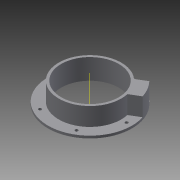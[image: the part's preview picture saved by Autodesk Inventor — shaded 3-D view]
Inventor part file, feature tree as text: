
AUTODESK INVENTOR PART (.ipt)
format: ipt  version: 2015 (Build 190159000, 159)  size: 134,656 bytes
history: native  units: in
note: dims shown in document units (in); Inventor stores cm internally (conversion verified against a paired STEP export)
features: sketch x5, extrude x3, hole x2, pattern_circular x2, plane x1
ambient origin geometry x8: Origin, YZ Plane, XZ Plane, XY Plane, X Axis, Y Axis, Z Axis, Center Point
bodies: Solid1 (feature_tree)
feature tree (13):
  extrude  "Extrusion1"  Depth=7.0in
  extrude  "Extrusion2"  Depth=0.2in
  hole  "Hole1"  [1 undecoded]
  pattern_circular  "Circular Pattern1"  [2 undecoded]
  extrude  "Extrusion3"  Depth=1.51in
  plane  "Work Plane2"
  hole  "Hole2"  [1 undecoded]
  pattern_circular  "Circular Pattern2"  [2 undecoded]
  sketch  "Sketch1"  dims[d0=4.81in d1=7.0in]
  sketch  "Sketch2"  dims[d2=0.2in d3=0.0in d4=5.21in]
  sketch  "Sketch3"  dims[d5=4.81in d6=1.51in d7=0.0in]
  sketch  "Sketch4"  dims[d8=0.895in]
  sketch  "Sketch5"  dims[d9=0.4475in d10=0.25in d11=0.3225in d12=0.25in d13=0.75in d14=0.375in d15=0.25in d16=0.5635in d17=1.0in d18=0.8108in d19=2.3622in d20=360.0deg d22=1.51in d23=0.0in d24=0.25in d25=0.25in d26=0.75in d27=0.375in d28=0.25in d29=0.5635in d30=1.1875in d31=0.0in d32=2.3622in d33=360.0deg]
note: 6 required parameter values undecoded (feature->parameter linkage not recoverable at this tier; creation-order binding heuristic only, values carry confidence <= 0.55)
